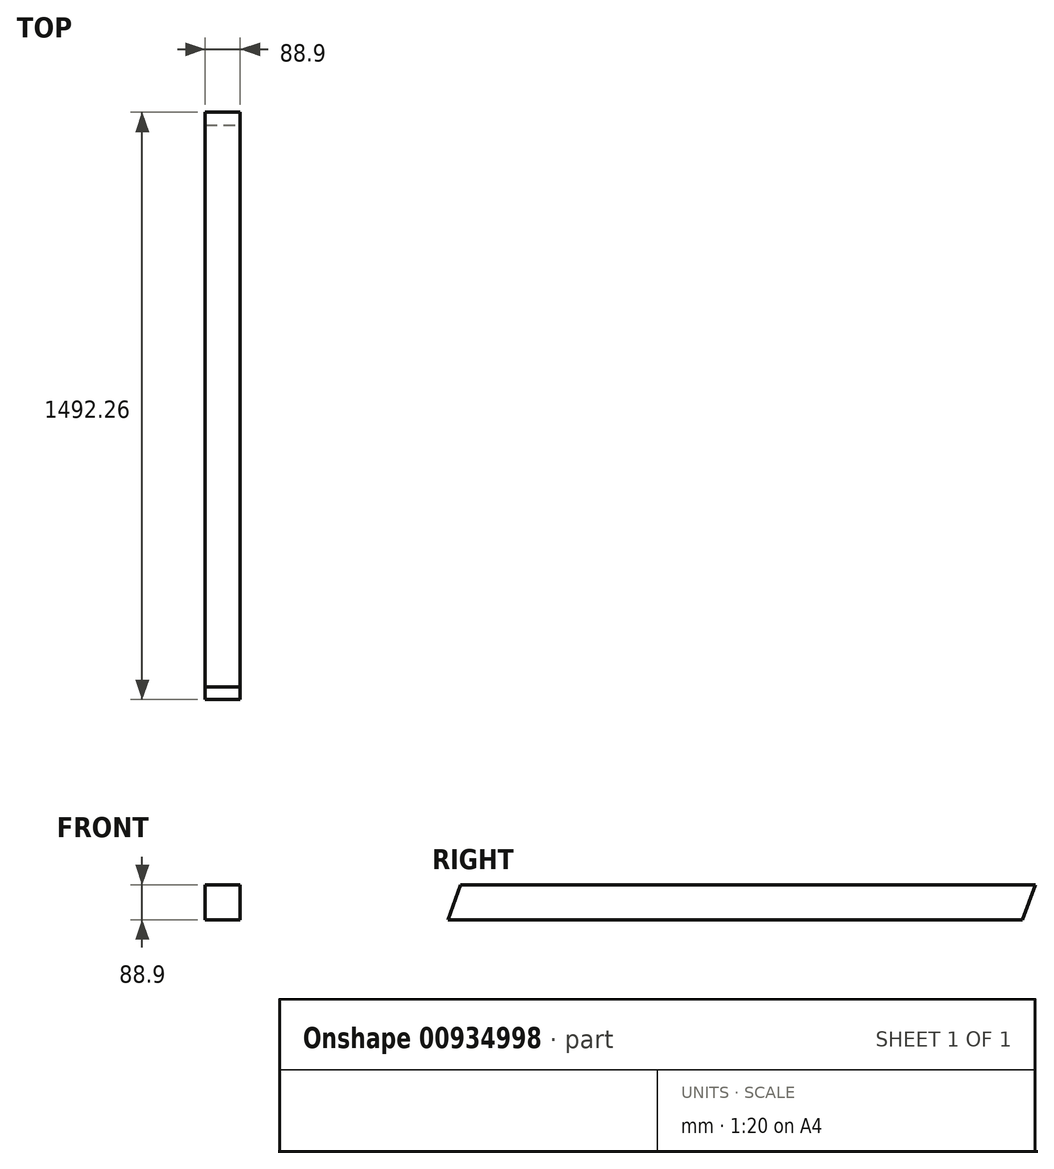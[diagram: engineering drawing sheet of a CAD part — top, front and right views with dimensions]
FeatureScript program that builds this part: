
annotation { "Feature Type Name" : "Feature", "Feature Type Description" : "" }
export const myFeature = defineFeature(function(context is Context, id is Id, definition is map)
    precondition{}
    {
        {
            var Q0;
            Q0=qCreatedBy(makeId("Front.planeOp"),FACE);
            var sketch = newSketch(context, id + "F0", { "sketchPlane" : qUnion([Q0])});
            skLineSegment(sketch, "E0.bottom", {"start": v(44.45, 44.45) * mm, "end": v(-44.45, 44.45) * mm});
            skLineSegment(sketch, "E0.top", {"start": v(44.45, -44.45) * mm, "end": v(-44.45, -44.45) * mm});
            skLineSegment(sketch, "E0.left", {"start": v(44.45, 44.45) * mm, "end": v(44.45, -44.45) * mm});
            skLineSegment(sketch, "E0.right", {"start": v(-44.45, 44.45) * mm, "end": v(-44.45, -44.45) * mm});
            skPoint(sketch, "E0.middle", {"position": v(0, 0) * mm});
            skSolve(sketch);
        }
        {
            var Q0;
            Q0 = qSketchRegion(id + "F0", true);
            extrude(context, id + "F1", {"entities" : qUnion([Q0]), "depth" : 1492.25 * mm, "offsetDistance" : 25.4 * mm, "symmetric" : true});
        }
        {
            var Q0;
            Q0=makeQuery(id+"F1.opExtrude","SWEPT_FACE",FACE,{"disambiguationData":[OSD([sQuery(id+"F0.wireOp",EDGE,"E0.left")])]});
            var sketch = newSketch(context, id + "F2", { "sketchPlane" : qUnion([Q0])});
            skLineSegment(sketch, "E1", {"start": v(-746.12, -44.45) * mm, "end": v(-746.12, 44.45) * mm});
            skLineSegment(sketch, "E2", {"start": v(-746.12, 44.45) * mm, "end": v(-713.77, 44.45) * mm});
            skLineSegment(sketch, "E3", {"start": v(-713.77, 44.45) * mm, "end": v(-746.12, -44.45) * mm});
            skLineSegment(sketch, "E4", {"start": v(746.12, 44.45) * mm, "end": v(746.12, -44.45) * mm});
            skLineSegment(sketch, "E5", {"start": v(746.12, -44.45) * mm, "end": v(713.77, -44.45) * mm});
            skLineSegment(sketch, "E6", {"start": v(713.77, -44.45) * mm, "end": v(746.12, 44.45) * mm});
            skSolve(sketch);
        }
        {
            var Q0;
            Q0 = qSketchRegion(id + "F2", true);
            extrude(context, id + "F3", {"entities" : qUnion([Q0]), "operationType" : NewBodyOperationType.REMOVE, "oppositeDirection" : true, "depth" : 508 * mm, "offsetDistance" : 25.4 * mm, "symmetric" : true});
        }
    });
